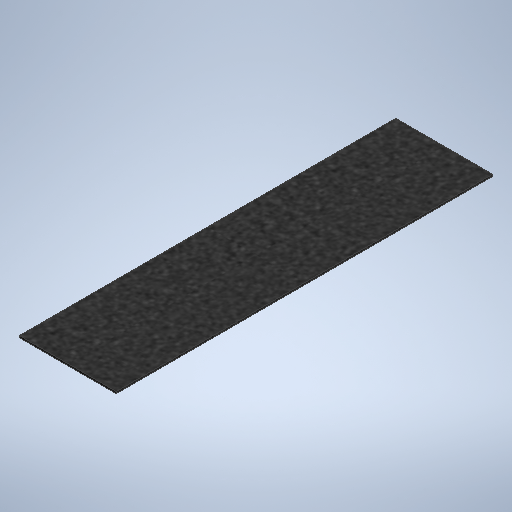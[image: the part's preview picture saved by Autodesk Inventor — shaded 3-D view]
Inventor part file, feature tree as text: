
AUTODESK INVENTOR PART (.ipt)
format: ipt  version: 2025 (Build 290162010, 162A)  size: 274,944 bytes
history: native  units: in
note: dims shown in document units (in); Inventor stores cm internally (conversion verified against a paired STEP export)
features: extrude x1, sketch x1
ambient origin geometry x8: Origin, YZ Plane, XZ Plane, XY Plane, X Axis, Y Axis, Z Axis, Center Point
bodies: Solid1 (feature_tree)
feature tree (2):
  extrude  "Extrusion1"  Depth=25.263in
  sketch  "Sketch1"  dims[d0=6.5in d1=25.263in d2=0.125in d3=0.0in]
